# Revit family: Auto-Door_Sliding_BiPart_CurtainWall_Tormax_TX9420
name_source: partatom
category: Doors
units: mm (PartAtom-declared; Revit-internal decimal feet)

## family parameters
Always vertical = Yes
Classification Number = 23.30.10.17.11
Cut with Voids When Loaded = No
Room Calculation Point = No
Shared = No

## types (8) — shared parameters
Analytic Construction = <None>
Assembly Code = B2030110
Available Options = [Standard Weatherstripping][Clean Room Seals][Electric Lock][Battery Backup][Door Position Monitoring][I/O Module][Key Switch]
Construction Details = http://www.arcat.com
Define Thermal Properties by = Schematic Type
Frame Thickness = 0' - 4 1/2"
Function = Interior
Glazing Stop Width = 0' - 0 1/4"
Green Building-LEED = http://www.arcat.com
Has Partial Breakout Capability = Yes
Keynote = 08463
Manufacturer = TORMAX USA Inc.
Manufacturer Fax = 210-494-5930
Manufacturer Website = http://www.tormaxusa.com
Miami Dade Conformance = Does Not Apply
Operating Temperature Range = Ambient -30F to 130F
Panel Thickness = 0' - 1 3/4"
Product Data = http://www.arcat.com
RO Spacing_Sides = 0' - 0 1/4"
RO Spacing_Top = 0' - 0 1/4"
Revision = R1_02-2014
Sales Information = http://www.tormaxusa.com
Send Message = http://www.arcat.com
Specification = http://www.arcat.com
Standards Conformance = ANSI A156.10  ;  NFPA 101  ;  UL325  ;  C-UL
Thickness = 0' - 4 1/2"
URL = http://www.tormaxusa.com
Water Penetration = as Specified
zero-valued in all types: Expected Lifespan (Years), Maintenance Schedule (Months), Warranty Duration (Years)

## per-type parameters (varying)
| type | Access Control | Description | HD Drive | Include Transom | Model | Transom Height | headerdepth |
| HD Access Control Glass Sidelight with no Transom | Yes | Tormax HD Automatic Sliding BiPart Door - Telescoping Access Controlled TX9420HDAC as Specified | Yes | No | TX9420HDAC as Specified | 0' - 0" | 1' - 1" |
| HD Access Control Glass Sidelight with Transom | Yes | Tormax HD Automatic Sliding BiPart Door - Telescoping Access Controlled TX9420HDAC as Specified | Yes | Yes | TX9420HDAC as Specified | 3' - 4" | 1' - 1" |
| HD Glass Sidelight with no Transom | No | Tormax HD Automatic Sliding BiPart Door - Telescoping TX9420HD as Specified | Yes | No | TX9420HD as Specified | 0' - 0" | 1' - 1" |
| HD Glass Sidelight with Transom | No | Tormax HD Automatic Sliding BiPart Door - Telescoping TX9420HD as Specified | Yes | Yes | TX9420HD as Specified | 3' - 4" | 1' - 1" |
| Access Control Glass Sidelight with no Transom | Yes | Tormax Automatic Sliding BiPart Door - Telescoping Access Controlled TX9420AC as Specified | No | No | TX9420AC as Specified | 0' - 0" | 0' - 11 5/8" |
| Access Control Glass Sidelight with Transom | Yes | Tormax Automatic Sliding BiPart Door - Telescoping Access Controlled TX9420AC as Specified | No | Yes | TX9420AC as Specified | 3' - 4" | 0' - 11 5/8" |
| Glass Sidelight with no Transom | No | Tormax Automatic Sliding BiPart Door - Telescoping TX9420 as Specified | No | No | TX9420 as Specified | 0' - 0" | 0' - 11 5/8" |
| Glass Sidelight with Transom | No | Tormax Automatic Sliding BiPart Door - Telescoping TX9420 as Specified | No | Yes | TX9420 as Specified | 3' - 4" | 0' - 11 5/8" |

## geometry (parser evidence)
native form markers: Blend x4, Sweep x6
no freeform markers — native parametric forms only
